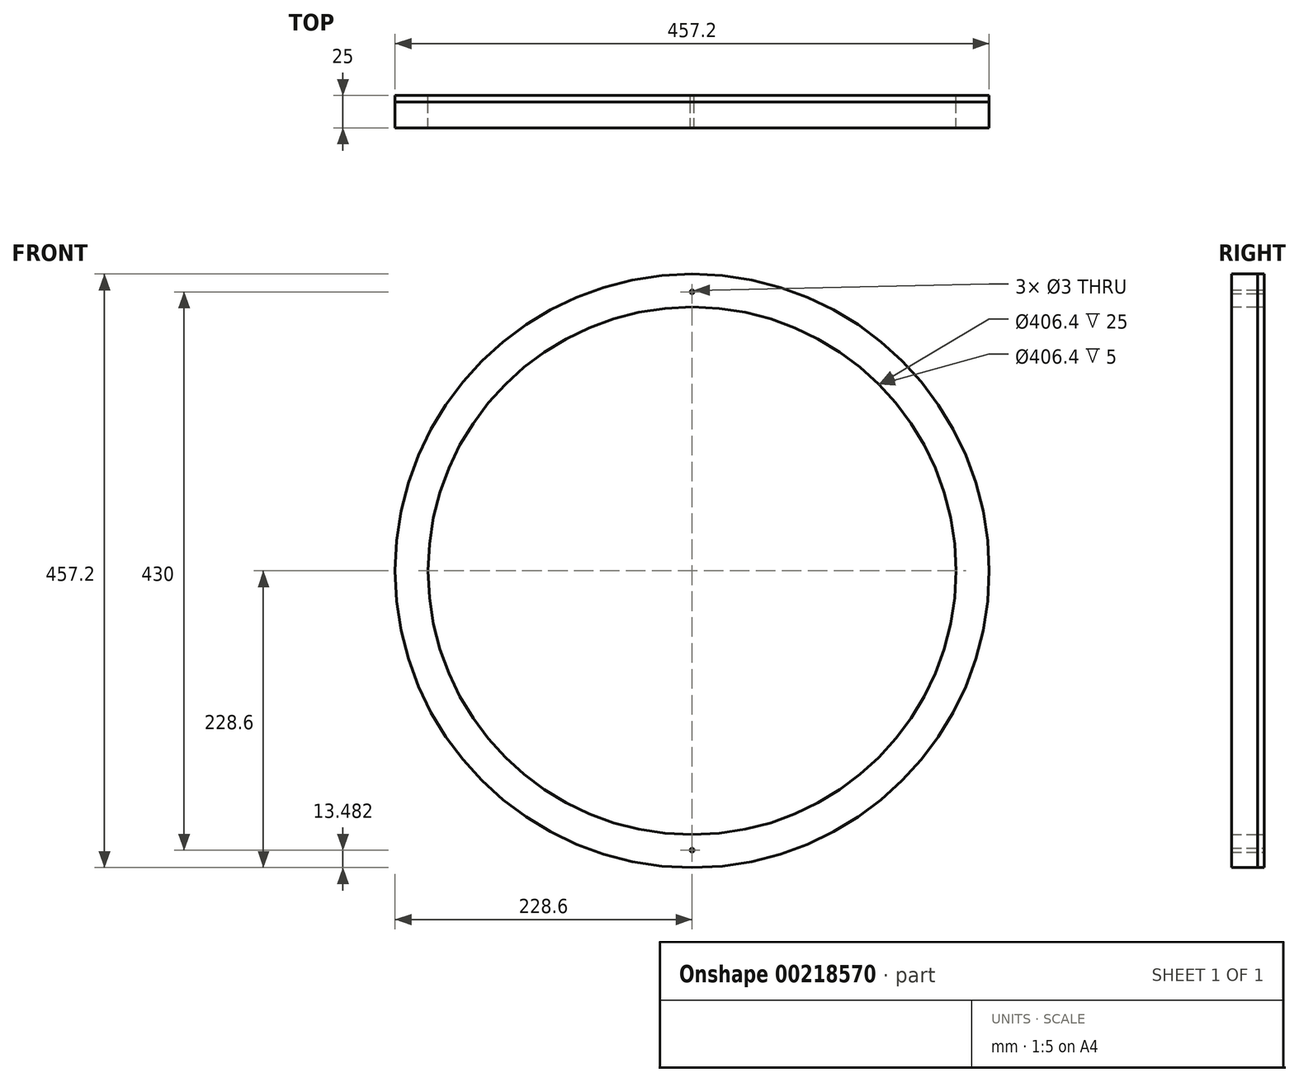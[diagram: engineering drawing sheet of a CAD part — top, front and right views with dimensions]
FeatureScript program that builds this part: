
annotation { "Feature Type Name" : "Feature", "Feature Type Description" : "" }
export const myFeature = defineFeature(function(context is Context, id is Id, definition is map)
    precondition{}
    {
        {
            var Q0;
            Q0=qCreatedBy(makeId("Front.planeOp"),FACE);
            var sketch = newSketch(context, id + "F0", { "sketchPlane" : qUnion([Q0])});
            skCircle(sketch, "E0", {"center": v(0, 0) * mm, "radius": 228.6 * mm});
            skCircle(sketch, "E1", {"center": v(0, 0) * mm, "radius": 203.2 * mm});
            skLineSegment(sketch, "E2", {"start": v(0, 238.57) * mm, "end": v(0, -228.6) * mm, "construction": true});
            skCircle(sketch, "E3", {"center": v(0, 214.88) * mm, "radius": 1.5 * mm});
            skCircle(sketch, "E4", {"center": v(0, -215.12) * mm, "radius": 1.5 * mm});
            skSolve(sketch);
        }
        {
            var Q0;
            Q0=makeQuery(id+"F0.imprint","IMPRINT",FACE,{"disambiguationData":[TD([[makeQuery(id+"F0.imprint","IMPRINT",EDGE,{"derivedFrom":sQuery(id+"F0.wireOp",EDGE,"E0")}),1.0]])]});
            var Q1;
            Q1=makeQuery(id+"F0.imprint","IMPRINT",FACE,{"disambiguationData":[TD([[makeQuery(id+"F0.imprint","IMPRINT",EDGE,{"derivedFrom":sQuery(id+"F0.wireOp",EDGE,"E4")}),1.0]])]});
            extrude(context, id + "F1", {"entities" : qUnion([Q0, Q1]), "depth" : 5 * mm});
        }
        {
            var Q0;
            Q0=qSketchRegion(id+"F0",true);
            extrude(context, id + "F2", {"entities" : qUnion([Q0]), "depth" : 25 * mm});
        }
    });
